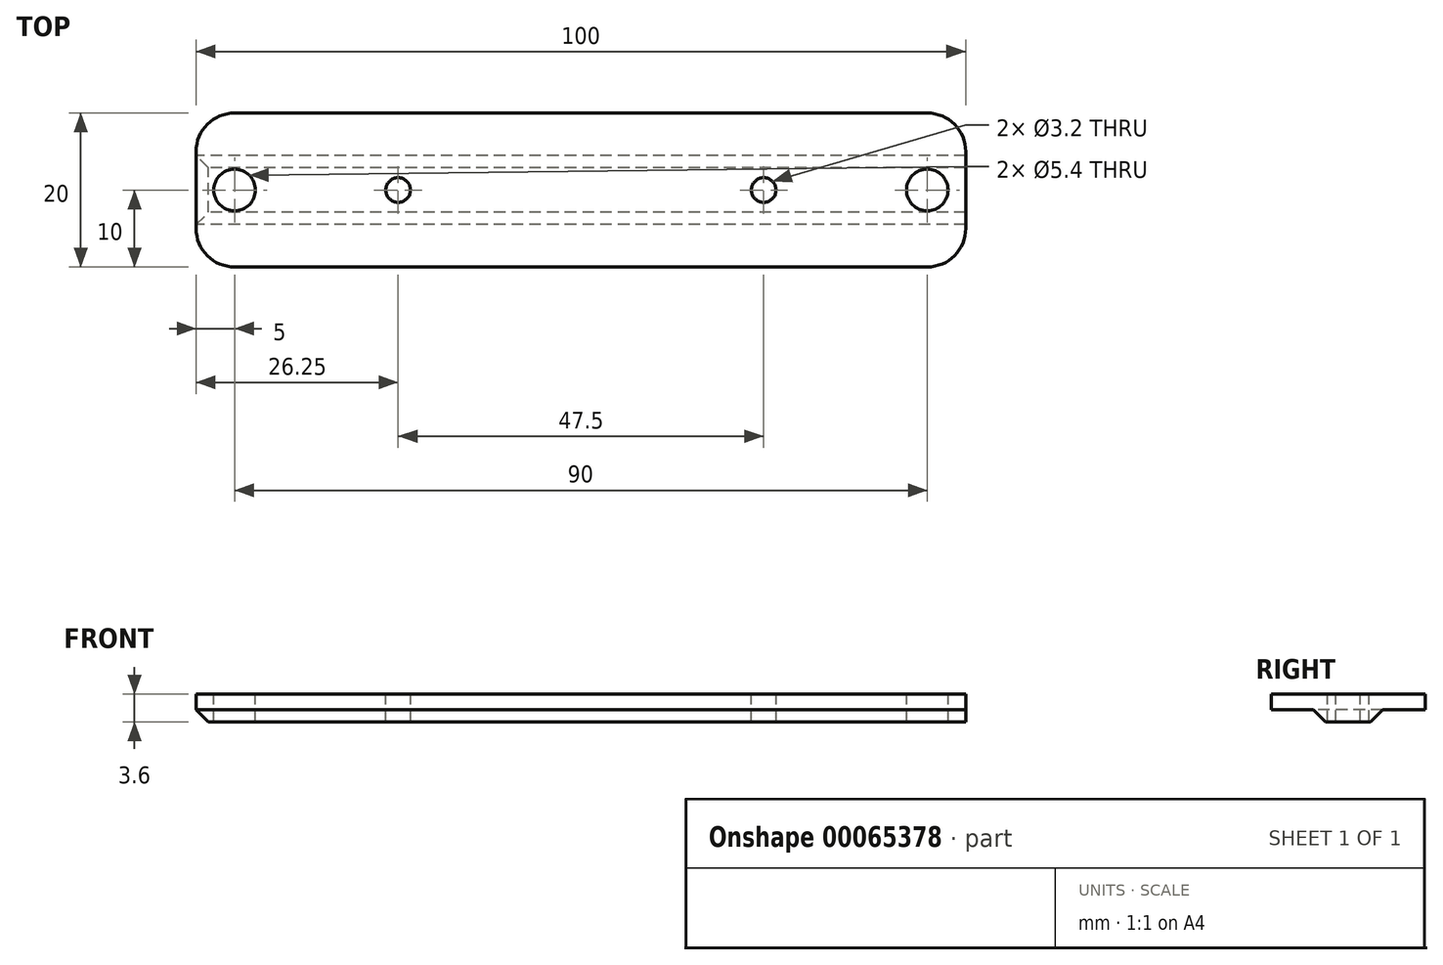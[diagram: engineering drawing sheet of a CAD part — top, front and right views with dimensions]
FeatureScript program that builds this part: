
annotation { "Feature Type Name" : "Feature", "Feature Type Description" : "" }
export const myFeature = defineFeature(function(context is Context, id is Id, definition is map)
    precondition{}
    {
        {
            var Q0;
            Q0=qCreatedBy(makeId("Top.planeOp"),FACE);
            var sketch = newSketch(context, id + "F0", { "sketchPlane" : qUnion([Q0])});
            skLineSegment(sketch, "E0.rect.bottom", {"start": v(45, 10) * mm, "end": v(-45, 10) * mm});
            skLineSegment(sketch, "E0.rect.top", {"start": v(45, -10) * mm, "end": v(-45, -10) * mm});
            skLineSegment(sketch, "E0.rect.left", {"start": v(50, 5) * mm, "end": v(50, -5) * mm});
            skLineSegment(sketch, "E0.rect.right", {"start": v(-50, 5) * mm, "end": v(-50, -5) * mm});
            skPoint(sketch, "E0.rect.middle", {"position": v(0, 0) * mm});
            skPoint(sketch, "E1.visualSharp", {"position": v(-50, 10) * mm});
            skArc(sketch, "E1.filletArc", {"start": v(-45, 10) * mm, "mid": v(-48.54, 8.54) * mm, "end": v(-50, 5) * mm});
            skPoint(sketch, "E2.visualSharp", {"position": v(50, 10) * mm});
            skArc(sketch, "E2.filletArc", {"start": v(50, 5) * mm, "mid": v(48.54, 8.54) * mm, "end": v(45, 10) * mm});
            skPoint(sketch, "E3.visualSharp", {"position": v(50, -10) * mm});
            skArc(sketch, "E3.filletArc", {"start": v(45, -10) * mm, "mid": v(48.54, -8.54) * mm, "end": v(50, -5) * mm});
            skPoint(sketch, "E4.visualSharp", {"position": v(-50, -10) * mm});
            skArc(sketch, "E4.filletArc", {"start": v(-50, -5) * mm, "mid": v(-48.54, -8.54) * mm, "end": v(-45, -10) * mm});
            skSolve(sketch);
        }
        {
            var Q0;
            Q0=qSketchRegion(id+"F0",true);
            extrude(context, id + "F1", {"entities" : qUnion([Q0]), "depth" : 2 * mm});
        }
        {
            var Q0;
            Q0=makeQuery(id+"F1.opExtrude","SWEPT_FACE",FACE,{"disambiguationData":[OSD([sQuery(id+"F0.wireOp",EDGE,"E0.rect.right")])]});
            var sketch = newSketch(context, id + "F2", { "sketchPlane" : qUnion([Q0])});
            skLineSegment(sketch, "E5", {"start": v(0, 0) * mm, "end": v(0, -1.6) * mm, "construction": true});
            skPoint(sketch, "E5.endSnap0", {"position": v(0, 0) * mm});
            skLineSegment(sketch, "E6", {"start": v(-2.9, -1.6) * mm, "end": v(2.9, -1.6) * mm});
            skLineSegment(sketch, "E7", {"start": v(-2.9, -1.6) * mm, "end": v(-4.5, 0) * mm});
            skLineSegment(sketch, "E8", {"start": v(-4.5, 0) * mm, "end": v(4.5, 0) * mm});
            skLineSegment(sketch, "E9", {"start": v(4.5, 0) * mm, "end": v(2.9, -1.6) * mm});
            skSolve(sketch);
        }
        {
            var Q0;
            Q0=qSketchRegion(id+"F2",true);
            var Q1;
            Q1=makeQuery(id+"F1.opExtrude","SWEPT_FACE",FACE,{"disambiguationData":[OSD([sQuery(id+"F0.wireOp",EDGE,"E0.rect.left")])]});
            extrude(context, id + "F3", {"entities" : qUnion([Q0]), "operationType" : NewBodyOperationType.ADD, "endBound" : BoundingType.UP_TO_SURFACE, "oppositeDirection" : true, "endBoundEntityFace" : qUnion([Q1]), "depth" : 25 * mm});
        }
        {
            var Q0;
            Q0=makeQuery(id+"F1.opExtrude","CAP_FACE",FACE,{"disambiguationData":[OSD([sQuery(id+"F0.wireOp",EDGE,"E0.rect.bottom"),sQuery(id+"F0.wireOp",EDGE,"E0.rect.top"),sQuery(id+"F0.wireOp",EDGE,"E0.rect.left"),sQuery(id+"F0.wireOp",EDGE,"E0.rect.right"),sQuery(id+"F0.wireOp",EDGE,"E1.filletArc"),sQuery(id+"F0.wireOp",EDGE,"E2.filletArc"),sQuery(id+"F0.wireOp",EDGE,"E3.filletArc"),sQuery(id+"F0.wireOp",EDGE,"E4.filletArc")])],"isStart":false});
            var sketch = newSketch(context, id + "F4", { "sketchPlane" : qUnion([Q0])});
            skLineSegment(sketch, "E10", {"start": v(-50, 0) * mm, "end": v(-45, 0) * mm, "construction": true});
            skLineSegment(sketch, "E11", {"start": v(-45, 0) * mm, "end": v(-23.75, 0) * mm, "construction": true});
            skLineSegment(sketch, "E12", {"start": v(-23.75, 0) * mm, "end": v(0, 0) * mm, "construction": true});
            skLineSegment(sketch, "E13", {"start": v(0, 0) * mm, "end": v(23.75, 0) * mm, "construction": true});
            skLineSegment(sketch, "E14", {"start": v(23.75, 0) * mm, "end": v(45, 0) * mm, "construction": true});
            skLineSegment(sketch, "E15", {"start": v(45, 0) * mm, "end": v(50, 0) * mm, "construction": true});
            skCircle(sketch, "E16", {"center": v(-45, 0) * mm, "radius": 2.7 * mm});
            skCircle(sketch, "E17", {"center": v(45, 0) * mm, "radius": 2.7 * mm});
            skCircle(sketch, "E18", {"center": v(23.75, 0) * mm, "radius": 1.6 * mm});
            skCircle(sketch, "E19", {"center": v(-23.75, 0) * mm, "radius": 1.6 * mm});
            skSolve(sketch);
        }
        {
            var Q0;
            Q0=qSketchRegion(id+"F4",true);
            extrude(context, id + "F5", {"entities" : qUnion([Q0]), "operationType" : NewBodyOperationType.REMOVE, "endBound" : BoundingType.THROUGH_ALL, "oppositeDirection" : true, "depth" : 25 * mm});
        }
        {
            var Q0;
            Q0=makeQuery(id+"F3.opExtrude","CAP_EDGE",EDGE,{"disambiguationData":[OSD([sQuery(id+"F2.wireOp",EDGE,"E6")])],"isStart":true});
            var Q1;
            Q1=makeQuery(id+"F3.opExtrude","TWEAK_EDGE",EDGE,{"derivedFrom":[makeQuery(id+"F1.opExtrude","SWEPT_FACE",FACE,{"disambiguationData":[OSD([sQuery(id+"F0.wireOp",EDGE,"E0.rect.left")])]}),makeQuery(id+"F2.imprint","IMPRINT",EDGE,{"derivedFrom":sQuery(id+"F2.wireOp",EDGE,"E6")})]});
            chamfer(context, id + "F6", {"entities" : qUnion([Q0, Q1]), "width" : 1.6 * mm, "tangentPropagation" : true});
        }
    });
